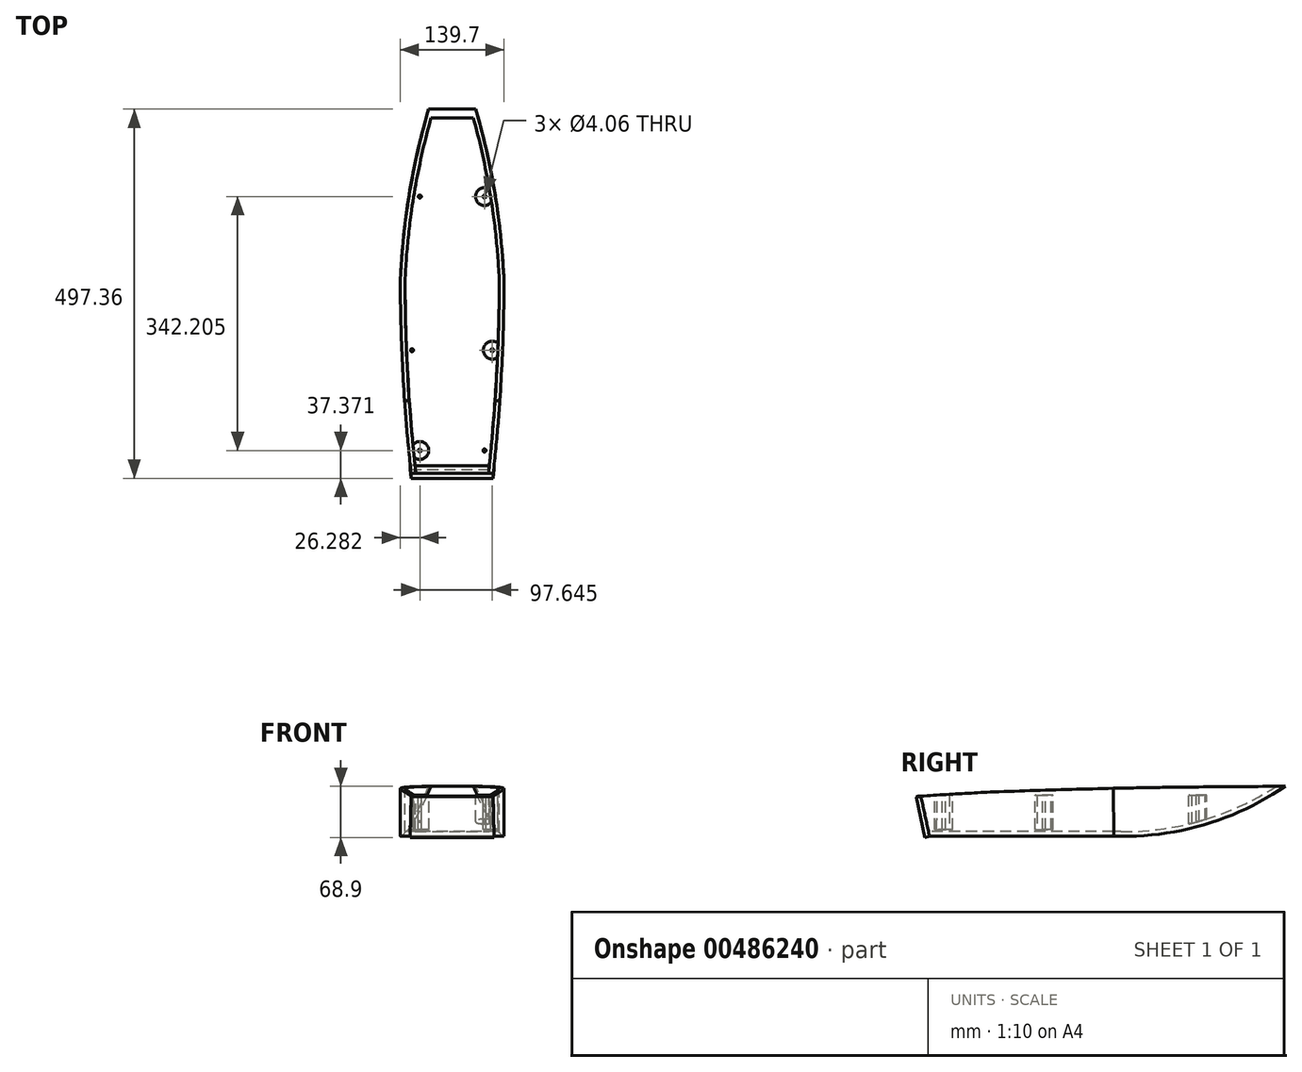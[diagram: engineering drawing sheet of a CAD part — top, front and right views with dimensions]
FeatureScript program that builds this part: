
annotation { "Feature Type Name" : "Feature", "Feature Type Description" : "" }
export const myFeature = defineFeature(function(context is Context, id is Id, definition is map)
    precondition{}
    {
        {
            var Q0;
            Q0=qCreatedBy(makeId("Right.planeOp"),FACE);
            var sketch = newSketch(context, id + "F0", { "sketchPlane" : qUnion([Q0])});
            skLineSegment(sketch, "E0", {"start": v(-327.18, -67.55) * mm, "end": v(-327.18, -4.05) * mm, "construction": true});
            skLineSegment(sketch, "E1", {"start": v(-321.08, -4.05) * mm, "end": v(186.9, 0) * mm});
            skArc(sketch, "E2", {"start": v(-34.33, -67.55) * mm, "mid": v(81.44, -50.66) * mm, "end": v(186.9, 0) * mm});
            skLineSegment(sketch, "E3", {"start": v(-34.33, -67.55) * mm, "end": v(-327.18, -67.55) * mm});
            skLineSegment(sketch, "E4", {"start": v(-327.18, -67.55) * mm, "end": v(-336.18, -4.05) * mm});
            skLineSegment(sketch, "E5", {"start": v(-336.18, -4.05) * mm, "end": v(-321.08, -4.05) * mm});
            skSolve(sketch);
        }
        {
            var Q0;
            Q0 = qSketchRegion(id + "F0", true);
            extrude(context, id + "F1", {"entities" : qUnion([Q0]), "depth" : 139.7 * mm, "offsetDistance" : 25.4 * mm});
        }
        {
            var Q0;
            Q0=makeQuery(id+"F1.opExtrude","SWEPT_FACE",FACE,{"disambiguationData":[OSD([sQuery(id+"F0.wireOp",EDGE,"E1")])]});
            var sketch = newSketch(context, id + "F2", { "sketchPlane" : qUnion([Q0])});
            skLineSegment(sketch, "E6", {"start": v(0, 186.9) * mm, "end": v(69.85, 186.9) * mm, "construction": true});
            skLineSegment(sketch, "E7", {"start": v(69.85, 186.9) * mm, "end": v(139.7, 186.9) * mm, "construction": true});
            skLineSegment(sketch, "E8", {"start": v(69.85, 186.9) * mm, "end": v(95.25, 186.9) * mm, "construction": true});
            skLineSegment(sketch, "E9", {"start": v(69.85, 186.9) * mm, "end": v(44.45, 186.9) * mm});
            skLineSegment(sketch, "E10", {"start": v(44.45, 186.9) * mm, "end": v(38.1, 186.9) * mm});
            skLineSegment(sketch, "E11", {"start": v(38.1, 186.9) * mm, "end": v(95.25, 186.9) * mm});
            skLineSegment(sketch, "E12", {"start": v(95.25, 186.9) * mm, "end": v(101.6, 186.9) * mm});
            skLineSegment(sketch, "E13", {"start": v(69.85, 186.9) * mm, "end": v(69.85, -36) * mm, "construction": true});
            skArc(sketch, "E14", {"start": v(38.1, 186.9) * mm, "mid": v(12.12, 72.28) * mm, "end": v(0, -44.62) * mm});
            skArc(sketch, "E15.MirrorCS", {"start": v(101.6, 186.9) * mm, "mid": v(127.58, 72.28) * mm, "end": v(139.7, -44.62) * mm});
            skArc(sketch, "E16", {"start": v(0, -44.62) * mm, "mid": v(4.72, -190.76) * mm, "end": v(18.37, -336.34) * mm});
            skArc(sketch, "E17.MirrorCS", {"start": v(139.7, -44.62) * mm, "mid": v(134.98, -190.76) * mm, "end": v(121.33, -336.34) * mm});
            skLineSegment(sketch, "E18", {"start": v(18.37, -336.34) * mm, "end": v(-216.12, -383.06) * mm});
            skLineSegment(sketch, "E19", {"start": v(-216.12, -383.06) * mm, "end": v(-36.2, 308.24) * mm});
            skLineSegment(sketch, "E20", {"start": v(-36.2, 308.24) * mm, "end": v(38.1, 186.9) * mm});
            skLineSegment(sketch, "E21", {"start": v(101.6, 186.9) * mm, "end": v(308.77, 281.19) * mm});
            skLineSegment(sketch, "E22", {"start": v(308.77, 281.19) * mm, "end": v(362.88, -384.41) * mm});
            skLineSegment(sketch, "E23", {"start": v(362.88, -384.41) * mm, "end": v(121.33, -336.34) * mm});
            skSolve(sketch);
        }
        {
            var Q0;
            Q0 = qSketchRegion(id + "F2", true);
            extrude(context, id + "F3", {"entities" : qUnion([Q0]), "operationType" : NewBodyOperationType.REMOVE, "oppositeDirection" : true, "depth" : 127 * mm, "offsetDistance" : 25.4 * mm});
        }
        {
            var Q0;
            Q0=makeQuery(id+"F3.boolean.opBoolean","COPY",FACE,{"derivedFrom":makeQuery(id+"F3.opExtrude","CAP_FACE",FACE,{"disambiguationData":[OSD([sQuery(id+"F2.wireOp",EDGE,"E14"),sQuery(id+"F2.wireOp",EDGE,"E16"),sQuery(id+"F2.wireOp",EDGE,"E18"),sQuery(id+"F2.wireOp",EDGE,"E19"),sQuery(id+"F2.wireOp",EDGE,"E20")])],"isStart":true})});
            var sketch = newSketch(context, id + "F4", { "sketchPlane" : qUnion([Q0])});
            skLineSegment(sketch, "E24", {"start": v(18.35, 336.19) * mm, "end": v(16.52, 321.1) * mm});
            skLineSegment(sketch, "E25", {"start": v(16.52, 321.1) * mm, "end": v(-10.34, 314.77) * mm});
            skLineSegment(sketch, "E26", {"start": v(-10.34, 314.77) * mm, "end": v(-10.34, 352.29) * mm});
            skLineSegment(sketch, "E27", {"start": v(-10.34, 352.29) * mm, "end": v(18.35, 336.19) * mm});
            skSolve(sketch);
        }
        {
            var Q0;
            {var subQ0=sQuery(id+"F2.wireOp",EDGE,"E16");var subQ1=makeQuery(id+"F3.opExtrude","CAP_FACE",FACE,{"disambiguationData":[OSD([sQuery(id+"F2.wireOp",EDGE,"E14"),subQ0,sQuery(id+"F2.wireOp",EDGE,"E18"),sQuery(id+"F2.wireOp",EDGE,"E19"),sQuery(id+"F2.wireOp",EDGE,"E20")])],"isStart":true});var subQ3=sQuery(id+"F0.wireOp",EDGE,"E4");Q0=makeQuery(id+"F4.imprint","IMPRINT",FACE,{"disambiguationData":[TD([[makeQuery(id+"F4.imprint","IMPRINT",EDGE,{"derivedFrom":makeQuery(id+"F3.boolean.opBoolean","INTERSECT",EDGE,{"derivedFrom":[makeQuery(id+"F1.opExtrude","SWEPT_FACE",FACE,{"disambiguationData":[OSD([subQ3])]}),subQ1]})}),1.0]])]});}
            var Q1;
            Q1=makeQuery(id+"F4.imprint","IMPRINT",FACE,{"disambiguationData":[TD([[makeQuery(id+"F4.imprint","IMPRINT",EDGE,{"derivedFrom":sQuery(id+"F4.wireOp",EDGE,"E25")}),-1.0]])]});
            extrude(context, id + "F5", {"entities" : qUnion([Q0, Q1]), "operationType" : NewBodyOperationType.REMOVE, "oppositeDirection" : true, "depth" : 25.4 * mm, "offsetDistance" : 25.4 * mm});
        }
        {
            var Q0;
            Q0=makeQuery(id+"F3.boolean.opBoolean","COPY",FACE,{"derivedFrom":makeQuery(id+"F3.opExtrude","CAP_FACE",FACE,{"disambiguationData":[OSD([sQuery(id+"F2.wireOp",EDGE,"E15.MirrorCS"),sQuery(id+"F2.wireOp",EDGE,"E17.MirrorCS"),sQuery(id+"F2.wireOp",EDGE,"E21"),sQuery(id+"F2.wireOp",EDGE,"E22"),sQuery(id+"F2.wireOp",EDGE,"E23")])],"isStart":true})});
            var sketch = newSketch(context, id + "F6", { "sketchPlane" : qUnion([Q0])});
            skLineSegment(sketch, "E28", {"start": v(123.18, 321.1) * mm, "end": v(121.35, 336.19) * mm});
            skLineSegment(sketch, "E29", {"start": v(121.35, 336.19) * mm, "end": v(123.18, 371.87) * mm});
            skLineSegment(sketch, "E30", {"start": v(123.18, 371.87) * mm, "end": v(171.77, 357.25) * mm});
            skLineSegment(sketch, "E31", {"start": v(171.77, 357.25) * mm, "end": v(136, 306.27) * mm});
            skLineSegment(sketch, "E32", {"start": v(136, 306.27) * mm, "end": v(123.18, 321.1) * mm});
            skSolve(sketch);
        }
        {
            var Q0;
            Q0 = qSketchRegion(id + "F6", true);
            extrude(context, id + "F7", {"entities" : qUnion([Q0]), "operationType" : NewBodyOperationType.REMOVE, "oppositeDirection" : true, "depth" : 25.4 * mm, "offsetDistance" : 25.4 * mm});
        }
        {
            var Q0;
            Q0=qCreatedBy(makeId("Right.planeOp"),FACE);
            var sketch = newSketch(context, id + "F8", { "sketchPlane" : qUnion([Q0])});
            skArc(sketch, "E33", {"start": v(186.5, 0) * mm, "mid": v(-73.96, -3.5) * mm, "end": v(-334.26, -13.22) * mm});
            skLineSegment(sketch, "E34", {"start": v(-334.26, -13.22) * mm, "end": v(-347.48, -6.61) * mm});
            skLineSegment(sketch, "E35", {"start": v(-347.48, -6.61) * mm, "end": v(-287.47, 51.36) * mm});
            skLineSegment(sketch, "E36", {"start": v(-287.47, 51.36) * mm, "end": v(186.5, 0) * mm});
            skSolve(sketch);
        }
        {
            var Q0;
            Q0 = qSketchRegion(id + "F8", true);
            extrude(context, id + "F9", {"entities" : qUnion([Q0]), "operationType" : NewBodyOperationType.REMOVE, "depth" : 635 * mm, "offsetDistance" : 25.4 * mm});
        }
        {
            var Q0;
            Q0=makeQuery(id+"F1.opExtrude","SWEPT_FACE",FACE,{"disambiguationData":[OSD([sQuery(id+"F0.wireOp",EDGE,"E1")])]});
            var Q1;
            Q1=makeQuery(id+"F9.boolean.opBoolean","COPY",FACE,{"derivedFrom":makeQuery(id+"F9.opExtrude","SWEPT_FACE",FACE,{"disambiguationData":[OSD([sQuery(id+"F8.wireOp",EDGE,"E33")])]})});
            shell(context, id + "F10", {"entities" : qUnion([Q0, Q1]), "thickness" : 6.35 * mm});
        }
        {
            var Q0;
            Q0=makeQuery(id+"F10.opShell","OFFSET_FACE",FACE,{"disambiguationData":[OSD([sQuery(id+"F0.wireOp",EDGE,"E4")])]});
            extrude(context, id + "F11", {"entities" : qUnion([Q0]), "operationType" : NewBodyOperationType.ADD, "depth" : 6.35 * mm, "offsetDistance" : 25.4 * mm});
        }
        {
            var Q0;
            Q0=qCreatedBy(makeId("Right.planeOp"),FACE);
            var sketch = newSketch(context, id + "F12", { "sketchPlane" : qUnion([Q0])});
            skLineSegment(sketch, "E37", {"start": v(-342.14, -13.44) * mm, "end": v(-304.04, -13.44) * mm});
            skLineSegment(sketch, "E38", {"start": v(-342.14, -69.25) * mm, "end": v(-304.04, -69.25) * mm});
            skLineSegment(sketch, "E39", {"start": v(-304.04, -13.44) * mm, "end": v(-291.91, -69.25) * mm});
            skLineSegment(sketch, "E40", {"start": v(-291.91, -69.25) * mm, "end": v(-304.04, -69.25) * mm});
            skLineSegment(sketch, "E41", {"start": v(-291.91, -69.25) * mm, "end": v(-304.04, -124.55) * mm});
            skLineSegment(sketch, "E42", {"start": v(-304.04, -124.55) * mm, "end": v(-384.25, -13.44) * mm});
            skLineSegment(sketch, "E43", {"start": v(-384.25, -13.44) * mm, "end": v(-363.45, 28.66) * mm});
            skLineSegment(sketch, "E44", {"start": v(-363.45, 28.66) * mm, "end": v(-304.04, -0.68) * mm});
            skLineSegment(sketch, "E45", {"start": v(-304.04, -0.68) * mm, "end": v(-304.04, -13.44) * mm});
            skSolve(sketch);
        }
        {
            var Q0;
            Q0 = qSketchRegion(id + "F12", true);
            extrude(context, id + "F13", {"entities" : qUnion([Q0]), "operationType" : NewBodyOperationType.REMOVE, "depth" : 635 * mm, "offsetDistance" : 25.4 * mm});
        }
        {
            var Q0;
            Q0=makeQuery(id+"F13.boolean.opBoolean","COPY",FACE,{"derivedFrom":makeQuery(id+"F13.opExtrude","SWEPT_FACE",FACE,{"disambiguationData":[OSD([sQuery(id+"F12.wireOp",EDGE,"E39")])]})});
            var sketch = newSketch(context, id + "F14", { "sketchPlane" : qUnion([Q0])});
            skLineSegment(sketch, "E46", {"start": v(14.57, 51.42) * mm, "end": v(125.13, 51.42) * mm});
            skLineSegment(sketch, "E47", {"start": v(125.13, 51.42) * mm, "end": v(126.36, -3.95) * mm});
            skLineSegment(sketch, "E48", {"start": v(126.36, -3.95) * mm, "end": v(13.34, -3.95) * mm});
            skLineSegment(sketch, "E49", {"start": v(13.34, -3.95) * mm, "end": v(14.57, 51.42) * mm});
            skSolve(sketch);
        }
        {
            var Q0;
            Q0 = qSketchRegion(id + "F14", true);
            extrude(context, id + "F15", {"entities" : qUnion([Q0]), "operationType" : NewBodyOperationType.ADD, "depth" : 6.35 * mm, "offsetDistance" : 25.4 * mm});
        }
        {
            var Q0;
            Q0=makeQuery(id+"F15.opExtrude","SWEPT_FACE",FACE,{"disambiguationData":[OSD([sQuery(id+"F14.wireOp",EDGE,"E46")])]});
            extrude(context, id + "F16", {"entities" : qUnion([Q0]), "operationType" : NewBodyOperationType.ADD, "depth" : 3.1 * mm, "offsetDistance" : 25.4 * mm});
        }
        {
            var Q0;
            Q0=qCreatedBy(makeId("Right.planeOp"),FACE);
            var sketch = newSketch(context, id + "F17", { "sketchPlane" : qUnion([Q0])});
            skArc(sketch, "E50", {"start": v(-44.6, -2.8) * mm, "mid": v(-180.74, -6.52) * mm, "end": v(-316.7, -14.24) * mm});
            skLineSegment(sketch, "E51", {"start": v(-316.7, -14.24) * mm, "end": v(-308.65, 94.54) * mm});
            skLineSegment(sketch, "E52", {"start": v(-308.65, 94.54) * mm, "end": v(-44.6, -2.8) * mm});
            skSolve(sketch);
        }
        {
            var Q0;
            Q0 = qSketchRegion(id + "F17", true);
            extrude(context, id + "F18", {"entities" : qUnion([Q0]), "operationType" : NewBodyOperationType.REMOVE, "depth" : 2540 * mm, "offsetDistance" : 25.4 * mm});
        }
        {
            var Q0;
            Q0=qCreatedBy(makeId("Top.planeOp"),FACE);
            cPlane(context, id + "F19", {"entities" : qUnion([Q0]), "cplaneType" : CPlaneType.OFFSET, "offset" : 12.2 * mm, "oppositeDirection" : true, "width" : 152.4 * mm, "height" : 152.4 * mm});
        }
        {
            var Q0;
            Q0=qCreatedBy(id+"F19.planeOp",FACE);
            var sketch = newSketch(context, id + "F20", { "sketchPlane" : qUnion([Q0])});
            skLineSegment(sketch, "E53.0", {"start": v(14.57, -304.06) * mm, "end": v(125.13, -304.06) * mm});
            skFitSpline(sketch, "E54.0", {"points": [v(12.11, -206.19) * mm, v(14.39, -238.86) * mm, v(17.34, -271.48) * mm, v(20.96, -304.04) * mm]});
            skFitSpline(sketch, "E55.0", {"points": [v(127.59, -206.19) * mm, v(125.31, -238.86) * mm, v(122.36, -271.48) * mm, v(118.74, -304.04) * mm]});
            skFitSpline(sketch, "E56.0", {"points": [v(6.35, -44.73) * mm, v(6.45, -98.68) * mm, v(8.37, -152.5) * mm, v(12.11, -206.19) * mm]});
            skFitSpline(sketch, "E57.0", {"points": [v(133.35, -44.73) * mm, v(133.25, -98.68) * mm, v(131.33, -152.5) * mm, v(127.59, -206.19) * mm]});
            skFitSpline(sketch, "E58.0", {"points": [v(14.46, 45.24) * mm, v(10.37, 15.37) * mm, v(7.66, -14.62) * mm, v(6.35, -44.73) * mm]});
            skFitSpline(sketch, "E59.0", {"points": [v(125.24, 45.24) * mm, v(126.26, 37.8) * mm, v(127.66, 26.61) * mm, v(129.28, 11.63) * mm, v(130.18, 2.23) * mm, v(130.83, -5.3) * mm, v(131.45, -12.82) * mm, v(132.13, -22.21) * mm, v(132.82, -33.48) * mm, v(133.19, -40.98) * mm, v(133.35, -44.73) * mm]});
            skEllipticalArc(sketch, "E60.0", {});
            skEllipticalArc(sketch, "E61.0", {});
            skCircle(sketch, "E62", {"center": v(26.28, -273.09) * mm, "radius": 2.03 * mm});
            skCircle(sketch, "E63", {"center": v(26.28, -273.09) * mm, "radius": 12.07 * mm});
            skLineSegment(sketch, "E64", {"start": v(12.11, -206.19) * mm, "end": v(57.88, -202.63) * mm, "construction": true});
            skCircle(sketch, "E65.MirrorC", {"center": v(15.77, -137.9) * mm, "radius": 12.07 * mm});
            skCircle(sketch, "E66.MirrorC", {"center": v(15.77, -137.9) * mm, "radius": 2.03 * mm});
            skLineSegment(sketch, "E67", {"start": v(7.14, -101.99) * mm, "end": v(49.25, -101.99) * mm, "construction": true});
            skCircle(sketch, "E68.MirrorC", {"center": v(26.28, 69.12) * mm, "radius": 12.07 * mm});
            skCircle(sketch, "E69.MirrorC", {"center": v(26.28, 69.12) * mm, "radius": 2.03 * mm});
            skLineSegment(sketch, "E70", {"start": v(69.85, -304.06) * mm, "end": v(69.85, -251.05) * mm, "construction": true});
            skCircle(sketch, "E71.MirrorC", {"center": v(113.42, -273.09) * mm, "radius": 12.07 * mm});
            skCircle(sketch, "E72.MirrorC", {"center": v(123.93, -137.9) * mm, "radius": 12.07 * mm});
            skCircle(sketch, "E73.MirrorC", {"center": v(113.42, 69.12) * mm, "radius": 12.07 * mm});
            skCircle(sketch, "E74.MirrorC", {"center": v(123.93, -137.9) * mm, "radius": 2.03 * mm});
            skCircle(sketch, "E75.MirrorC", {"center": v(113.42, -273.09) * mm, "radius": 2.03 * mm});
            skCircle(sketch, "E76.MirrorC", {"center": v(113.42, 69.12) * mm, "radius": 2.03 * mm});
            const initialGuessF20  = {"E60.0": [-0.842279880137066, -0.08731569305445422, 1, 0, 0.9765583119211965, 0.9765273127267434, 0.13615791579696543, 0.2722729261998068], "E61.0": [0.9819798801370647, -0.08731569305445412, -1, 0, 0.976558311921195, 0.976527312726742, 6.0109123809797795, 6.147027391382621], "E60.0": [-0.842279880137066, -0.08731569305445422, 1, 0, 0.9765583119211965, 0.9765273127267434, 0.13615791579696543, 0.2722729261998068]};
            skSetInitialGuess(sketch, initialGuessF20);
            skSolve(sketch);
        }
        {
            var Q0;
            Q0=makeQuery(id+"F20.imprint","IMPRINT",FACE,{"disambiguationData":[TD([[makeQuery(id+"F20.imprint","IMPRINT",EDGE,{"derivedFrom":sQuery(id+"F20.wireOp",EDGE,"E66.MirrorC")}),1.0]])]});
            var Q1;
            Q1=makeQuery(id+"F20.imprint","IMPRINT",FACE,{"disambiguationData":[TD([[makeQuery(id+"F20.imprint","IMPRINT",EDGE,{"derivedFrom":sQuery(id+"F20.wireOp",EDGE,"E62")}),-1.0]])]});
            var Q2;
            Q2=makeQuery(id+"F20.imprint","IMPRINT",FACE,{"disambiguationData":[TD([[makeQuery(id+"F20.imprint","IMPRINT",EDGE,{"derivedFrom":sQuery(id+"F20.wireOp",EDGE,"E74.MirrorC")}),-1.0]])]});
            var Q3;
            Q3=makeQuery(id+"F20.imprint","IMPRINT",FACE,{"disambiguationData":[TD([[makeQuery(id+"F20.imprint","IMPRINT",EDGE,{"derivedFrom":sQuery(id+"F20.wireOp",EDGE,"E75.MirrorC")}),1.0]])]});
            extrude(context, id + "F21", {"entities" : qUnion([Q0, Q1, Q2, Q3]), "operationType" : NewBodyOperationType.ADD, "oppositeDirection" : true, "depth" : 46.23 * mm, "offsetDistance" : 25.4 * mm});
        }
        {
            var Q0;
            Q0=makeQuery(id+"F20.imprint","IMPRINT",FACE,{"disambiguationData":[TD([[makeQuery(id+"F20.imprint","IMPRINT",EDGE,{"derivedFrom":sQuery(id+"F20.wireOp",EDGE,"E76.MirrorC")}),-1.0]])]});
            var Q1;
            Q1=makeQuery(id+"F20.imprint","IMPRINT",FACE,{"disambiguationData":[TD([[makeQuery(id+"F20.imprint","IMPRINT",EDGE,{"derivedFrom":sQuery(id+"F20.wireOp",EDGE,"E69.MirrorC")}),1.0]])]});
            var Q2;
            Q2=sQuery(id+"F20.wireOp",EDGE,"E68.MirrorC");
            var Q3;
            Q3=sQuery(id+"F20.wireOp",EDGE,"E73.MirrorC");
            var Q4;
            Q4=sQuery(id+"F20.wireOp",EDGE,"E76.MirrorC");
            var Q5;
            Q5=sQuery(id+"F20.wireOp",EDGE,"E69.MirrorC");
            extrude(context, id + "F22", {"entities" : qUnion([Q0, Q1]), "operationType" : NewBodyOperationType.ADD, "surfaceEntities" : qUnion([Q2, Q3, Q4, Q5]), "oppositeDirection" : true, "depth" : 38.35 * mm, "offsetDistance" : 25.4 * mm});
        }
    });
